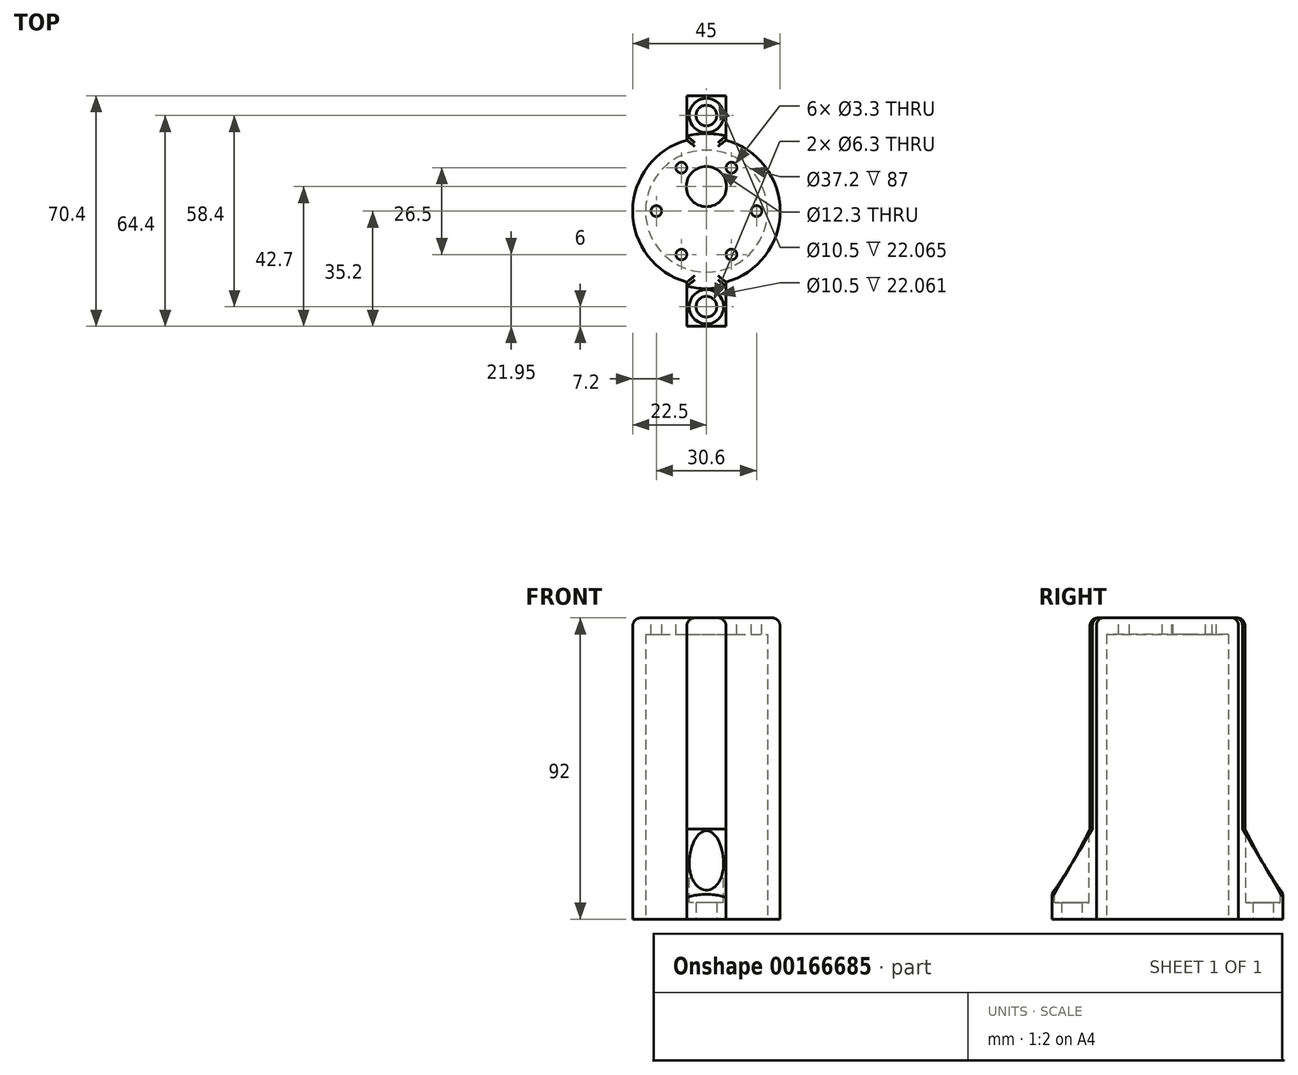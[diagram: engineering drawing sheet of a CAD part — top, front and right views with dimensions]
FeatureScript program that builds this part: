
annotation { "Feature Type Name" : "Feature", "Feature Type Description" : "" }
export const myFeature = defineFeature(function(context is Context, id is Id, definition is map)
    precondition{}
    {
        {
            assignVariable(context, id + "F0", {"name" : "Length", "anyValue" : 92});
        }
        {
            var Q0;
            Q0=qCreatedBy(makeId("Top.planeOp"),FACE);
            var sketch = newSketch(context, id + "F1", { "sketchPlane" : qUnion([Q0])});
            skLineSegment(sketch, "E0.bottom", {"start": v(-6, 35.2) * mm, "end": v(6, 35.2) * mm});
            skCircle(sketch, "E1", {"center": v(0, 29.2) * mm, "radius": 3.15 * mm});
            skCircle(sketch, "E2", {"center": v(0, 0) * mm, "radius": 22.5 * mm});
            skLineSegment(sketch, "E3", {"start": v(-6, 35.2) * mm, "end": v(-6, 21.69) * mm});
            skLineSegment(sketch, "E4", {"start": v(6, 21.69) * mm, "end": v(6, 35.2) * mm});
            skLineSegment(sketch, "E5.1.0", {"start": v(-6, -21.69) * mm, "end": v(-6, -35.2) * mm});
            skLineSegment(sketch, "E5.1.1", {"start": v(6, -35.2) * mm, "end": v(6, -21.69) * mm});
            skLineSegment(sketch, "E5.1.2", {"start": v(6, -35.2) * mm, "end": v(-6, -35.2) * mm});
            skCircle(sketch, "E5.1.3", {"center": v(0, -29.2) * mm, "radius": 3.15 * mm});
            skSolve(sketch);
        }
        {
            var Q0;
            Q0 = qSketchRegion(id + "F1", true);
            extrude(context, id + "F2", {"entities" : qUnion([Q0]), "depth" : (getVariable(context, 'Length')) * mm});
        }
        {
            var Q0;
            Q0=makeQuery(id+"F2.opExtrude","CAP_FACE",FACE,{"disambiguationData":[OSD([sQuery(id+"F1.wireOp",EDGE,"E0.bottom"),sQuery(id+"F1.wireOp",EDGE,"E1"),sQuery(id+"F1.wireOp",EDGE,"E2"),sQuery(id+"F1.wireOp",EDGE,"E3"),sQuery(id+"F1.wireOp",EDGE,"E4"),sQuery(id+"F1.wireOp",EDGE,"E5.1.0"),sQuery(id+"F1.wireOp",EDGE,"E5.1.1"),sQuery(id+"F1.wireOp",EDGE,"E5.1.2"),sQuery(id+"F1.wireOp",EDGE,"E5.1.3"),sQuery(id+"F1.wireOp",EDGE,"E5.2.0"),sQuery(id+"F1.wireOp",EDGE,"E5.2.1"),sQuery(id+"F1.wireOp",EDGE,"E5.2.2"),sQuery(id+"F1.wireOp",EDGE,"E5.2.3")])],"isStart":true});
            var sketch = newSketch(context, id + "F3", { "sketchPlane" : qUnion([Q0])});
            skCircle(sketch, "E6", {"center": v(0, 0) * mm, "radius": 18.6 * mm});
            skSolve(sketch);
        }
        {
            var Q0;
            Q0=makeQuery(id+"F2.opExtrude","CAP_FACE",FACE,{"disambiguationData":[OSD([sQuery(id+"F1.wireOp",EDGE,"E0.bottom"),sQuery(id+"F1.wireOp",EDGE,"E1"),sQuery(id+"F1.wireOp",EDGE,"E2"),sQuery(id+"F1.wireOp",EDGE,"E3"),sQuery(id+"F1.wireOp",EDGE,"E4"),sQuery(id+"F1.wireOp",EDGE,"E5.1.0"),sQuery(id+"F1.wireOp",EDGE,"E5.1.1"),sQuery(id+"F1.wireOp",EDGE,"E5.1.2"),sQuery(id+"F1.wireOp",EDGE,"E5.1.3"),sQuery(id+"F1.wireOp",EDGE,"E5.2.0"),sQuery(id+"F1.wireOp",EDGE,"E5.2.1"),sQuery(id+"F1.wireOp",EDGE,"E5.2.2"),sQuery(id+"F1.wireOp",EDGE,"E5.2.3")])],"isStart":false});
            var sketch = newSketch(context, id + "F4", { "sketchPlane" : qUnion([Q0])});
            skCircle(sketch, "E7", {"center": v(0, 7.5) * mm, "radius": 6.15 * mm});
            skCircle(sketch, "E8", {"center": v(-15.3, 0) * mm, "radius": 1.65 * mm});
            skCircle(sketch, "E9.1.0", {"center": v(-7.65, -13.25) * mm, "radius": 1.65 * mm});
            skCircle(sketch, "E9.2.0", {"center": v(7.65, -13.25) * mm, "radius": 1.65 * mm});
            skCircle(sketch, "E9.3.0", {"center": v(15.3, 0) * mm, "radius": 1.65 * mm});
            skCircle(sketch, "E9.4.0", {"center": v(7.65, 13.25) * mm, "radius": 1.65 * mm});
            skCircle(sketch, "E9.5.0", {"center": v(-7.65, 13.25) * mm, "radius": 1.65 * mm});
            skPoint(sketch, "E9.center", {"position": v(0, 0) * mm});
            skSolve(sketch);
        }
        {
            var Q0;
            Q0 = qSketchRegion(id + "F3", true);
            extrude(context, id + "F5", {"entities" : qUnion([Q0]), "operationType" : NewBodyOperationType.REMOVE, "oppositeDirection" : true, "depth" : (getVariable(context, 'Length') - 5) * mm});
        }
        {
            var Q0;
            Q0=qCreatedBy(makeId("Right.planeOp"),FACE);
            var sketch = newSketch(context, id + "F6", { "sketchPlane" : qUnion([Q0])});
            skLineSegment(sketch, "E10", {"start": v(23.69, 102) * mm, "end": v(23.69, 27.52) * mm});
            skLineSegment(sketch, "E11", {"start": v(23.69, 27.52) * mm, "end": v(36.69, 5) * mm});
            skLineSegment(sketch, "E12", {"start": v(36.69, 5) * mm, "end": v(36.69, 102) * mm});
            skLineSegment(sketch, "E13", {"start": v(36.69, 102) * mm, "end": v(23.69, 102) * mm});
            skLineSegment(sketch, "E14", {"start": v(0, 0) * mm, "end": v(0, 102.48) * mm, "construction": true});
            skSolve(sketch);
        }
        {
            var Q0;
            Q0 = qSketchRegion(id + "F6", true);
            var Q1;
            Q1=sQuery(id+"F6.wireOp",EDGE,"E14");
            revolve(context, id + "F7", {"operationType" : NewBodyOperationType.REMOVE, "entities" : qUnion([Q0]), "axis" : qUnion([Q1]), "revolveType" : RevolveType.FULL, "oppositeDirection" : true});
        }
        {
            var Q0;
            Q0 = qSketchRegion(id + "F4", true);
            extrude(context, id + "F8", {"entities" : qUnion([Q0]), "operationType" : NewBodyOperationType.REMOVE, "endBound" : BoundingType.THROUGH_ALL, "oppositeDirection" : true, "depth" : 25 * mm});
        }
        {
            var Q0;
            Q0=makeQuery(id+"F2.opExtrude","CAP_FACE",FACE,{"disambiguationData":[OSD([sQuery(id+"F1.wireOp",EDGE,"E0.bottom"),sQuery(id+"F1.wireOp",EDGE,"E1"),sQuery(id+"F1.wireOp",EDGE,"E2"),sQuery(id+"F1.wireOp",EDGE,"E3"),sQuery(id+"F1.wireOp",EDGE,"E4"),sQuery(id+"F1.wireOp",EDGE,"E5.1.0"),sQuery(id+"F1.wireOp",EDGE,"E5.1.1"),sQuery(id+"F1.wireOp",EDGE,"E5.1.2"),sQuery(id+"F1.wireOp",EDGE,"E5.1.3"),sQuery(id+"F1.wireOp",EDGE,"E5.2.0"),sQuery(id+"F1.wireOp",EDGE,"E5.2.1"),sQuery(id+"F1.wireOp",EDGE,"E5.2.2"),sQuery(id+"F1.wireOp",EDGE,"E5.2.3")])],"isStart":false});
            var sketch = newSketch(context, id + "F9", { "sketchPlane" : qUnion([Q0])});
            skCircle(sketch, "E15", {"center": v(0, 29.2) * mm, "radius": 5.25 * mm});
            skCircle(sketch, "E16", {"center": v(0, -29.2) * mm, "radius": 5.25 * mm});
            skSolve(sketch);
        }
        {
            var Q0;
            Q0 = qSketchRegion(id + "F9", true);
            extrude(context, id + "F10", {"entities" : qUnion([Q0]), "operationType" : NewBodyOperationType.REMOVE, "oppositeDirection" : true, "depth" : (getVariable(context, 'Length') - 5) * mm});
        }
        {
            var Q0;
            {var subQ0=sQuery(id+"F1.wireOp",EDGE,"E2");Q0=makeQuery(id+"F2.opExtrude","CAP_EDGE",EDGE,{"disambiguationData":[OSD([subQ0]),TDD([makeQuery(id+"F1.imprint","IMPRINT",EDGE,{"disambiguationData":[TD([[makeQuery(id+"F1.imprint","INTERSECT",VERTEX,{"derivedFrom":[subQ0,sQuery(id+"F1.wireOp",EDGE,"E3")]}),-1.0]])],"derivedFrom":subQ0})])],"isStart":false});}
            var Q1;
            Q1=makeQuery(id+"F2.opExtrude","CAP_EDGE",EDGE,{"disambiguationData":[OSD([sQuery(id+"F1.wireOp",EDGE,"E5.1.0")])],"isStart":false});
            var Q2;
            Q2=makeQuery(id+"F7.boolean.opBoolean","INTERSECT",EDGE,{"disambiguationData":[OD(1.0)],"derivedFrom":[makeQuery(id+"F2.opExtrude","CAP_FACE",FACE,{"disambiguationData":[OSD([sQuery(id+"F1.wireOp",EDGE,"E0.bottom"),sQuery(id+"F1.wireOp",EDGE,"E1"),sQuery(id+"F1.wireOp",EDGE,"E2"),sQuery(id+"F1.wireOp",EDGE,"E3"),sQuery(id+"F1.wireOp",EDGE,"E4"),sQuery(id+"F1.wireOp",EDGE,"E5.1.0"),sQuery(id+"F1.wireOp",EDGE,"E5.1.1"),sQuery(id+"F1.wireOp",EDGE,"E5.1.2"),sQuery(id+"F1.wireOp",EDGE,"E5.1.3")])],"isStart":false}),makeQuery(id+"F7.opRevolve","SWEPT_FACE",FACE,{"disambiguationData":[OSD([sQuery(id+"F6.wireOp",EDGE,"E10")])]})]});
            var Q3;
            Q3=makeQuery(id+"F2.opExtrude","CAP_EDGE",EDGE,{"disambiguationData":[OSD([sQuery(id+"F1.wireOp",EDGE,"E5.1.1")])],"isStart":false});
            var Q4;
            {var subQ0=sQuery(id+"F1.wireOp",EDGE,"E2");Q4=makeQuery(id+"F2.opExtrude","CAP_EDGE",EDGE,{"disambiguationData":[OSD([subQ0]),TDD([makeQuery(id+"F1.imprint","IMPRINT",EDGE,{"disambiguationData":[TD([[makeQuery(id+"F1.imprint","INTERSECT",VERTEX,{"derivedFrom":[subQ0,sQuery(id+"F1.wireOp",EDGE,"E4")]}),1.0]])],"derivedFrom":subQ0})])],"isStart":false});}
            var Q5;
            Q5=makeQuery(id+"F2.opExtrude","CAP_EDGE",EDGE,{"disambiguationData":[OSD([sQuery(id+"F1.wireOp",EDGE,"E4")])],"isStart":false});
            var Q6;
            Q6=makeQuery(id+"F7.boolean.opBoolean","INTERSECT",EDGE,{"disambiguationData":[OD(0.0)],"derivedFrom":[makeQuery(id+"F2.opExtrude","CAP_FACE",FACE,{"disambiguationData":[OSD([sQuery(id+"F1.wireOp",EDGE,"E0.bottom"),sQuery(id+"F1.wireOp",EDGE,"E1"),sQuery(id+"F1.wireOp",EDGE,"E2"),sQuery(id+"F1.wireOp",EDGE,"E3"),sQuery(id+"F1.wireOp",EDGE,"E4"),sQuery(id+"F1.wireOp",EDGE,"E5.1.0"),sQuery(id+"F1.wireOp",EDGE,"E5.1.1"),sQuery(id+"F1.wireOp",EDGE,"E5.1.2"),sQuery(id+"F1.wireOp",EDGE,"E5.1.3")])],"isStart":false}),makeQuery(id+"F7.opRevolve","SWEPT_FACE",FACE,{"disambiguationData":[OSD([sQuery(id+"F6.wireOp",EDGE,"E10")])]})]});
            var Q7;
            Q7=makeQuery(id+"F2.opExtrude","CAP_EDGE",EDGE,{"disambiguationData":[OSD([sQuery(id+"F1.wireOp",EDGE,"E3")])],"isStart":false});
            fillet(context, id + "F11", {"entities" : qUnion([Q0, Q1, Q2, Q3, Q4, Q5, Q6, Q7]), "radius" : 2.5 * mm, "tangentPropagation" : true, "allowEdgeOverflow" : false});
        }
    });
